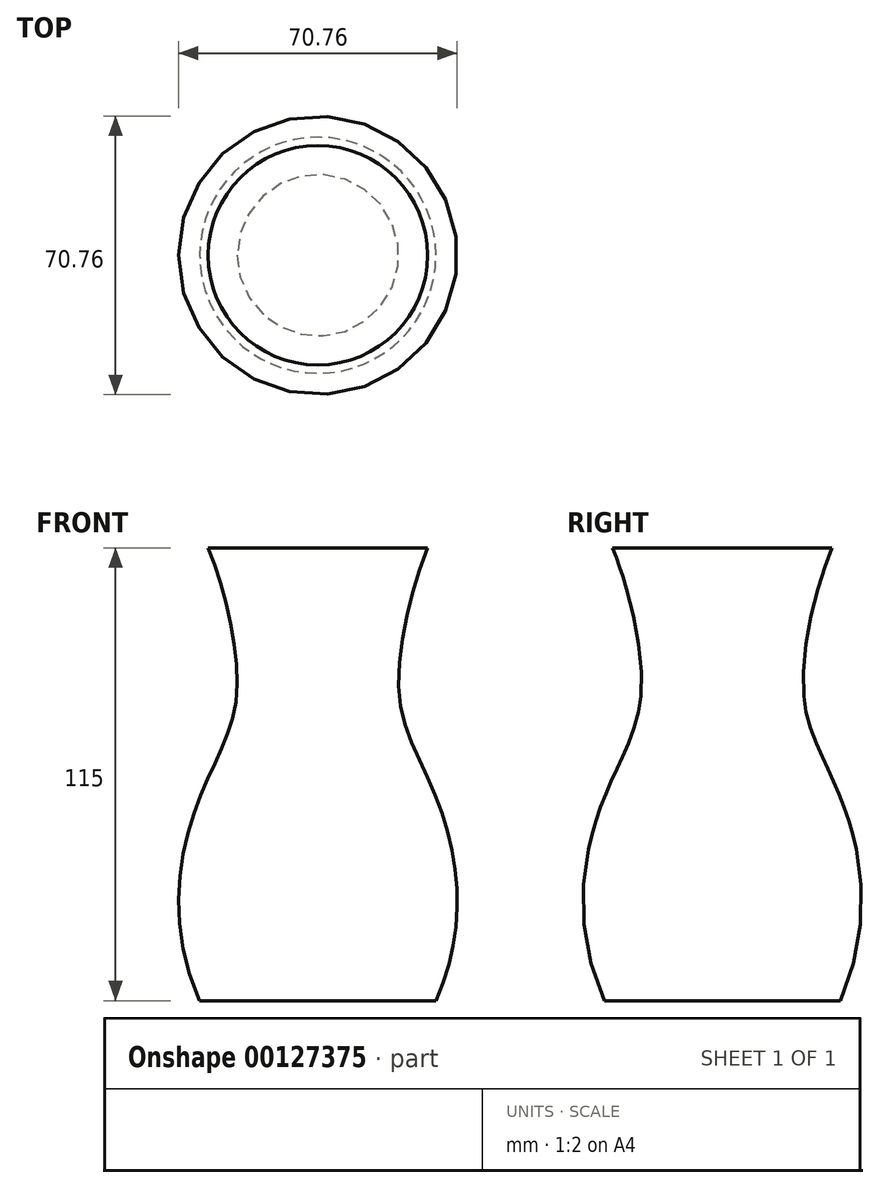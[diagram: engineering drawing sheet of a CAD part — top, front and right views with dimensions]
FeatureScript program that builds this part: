
annotation { "Feature Type Name" : "Feature", "Feature Type Description" : "" }
export const myFeature = defineFeature(function(context is Context, id is Id, definition is map)
    precondition{}
    {
        {
            var Q0;
            Q0=qCreatedBy(makeId("Front.planeOp"),FACE);
            var sketch = newSketch(context, id + "F0", { "sketchPlane" : qUnion([Q0])});
            skLineSegment(sketch, "E0", {"start": v(0, 0) * mm, "end": v(30, 0) * mm});
            skLineSegment(sketch, "E1", {"start": v(0, 0) * mm, "end": v(0, 115) * mm});
            skFitSpline(sketch, "E2", {"points": [v(30, 0) * mm, v(30, 51.66) * mm, v(20.65, 77.6) * mm, v(27.87, 115) * mm], "startDerivative": vector(69, 154.73) * mm, "endDerivative": vector(36.08, 91.05) * mm});
            skLineSegment(sketch, "E3", {"start": v(0, 115) * mm, "end": v(27.87, 115) * mm});
            skSolve(sketch);
        }
        {
            var Q0;
            Q0 = qSketchRegion(id + "F0", true);
            var Q1;
            Q1=sQuery(id+"F0.wireOp",EDGE,"E1");
            revolve(context, id + "F1", {"entities" : qUnion([Q0]), "axis" : qUnion([Q1]), "revolveType" : RevolveType.FULL});
        }
    });
